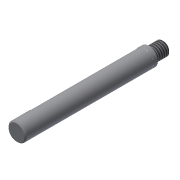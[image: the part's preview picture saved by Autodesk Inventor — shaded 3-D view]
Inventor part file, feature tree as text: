
AUTODESK INVENTOR PART (.ipt)
format: ipt  version: 2015 (Build 190159000, 159)  size: 125,440 bytes
history: native  units: mm
features: extrude x8, sketch x8, chamfer x3, thread x1
ambient origin geometry x8: Origin, YZ Plane, XZ Plane, XY Plane, X Axis, Y Axis, Z Axis, Center Point
bodies: Solid1 (feature_tree)
feature tree (20):
  extrude  "Extrusion1"  Depth=65.0mm TaperAngle=0.0deg
  extrude  "Extrusion2"  Depth=8.5mm TaperAngle=0.0deg
  extrude  "Extrusion3"  Depth=8.5mm TaperAngle=0.0deg
  extrude  "Extrusion4"  Depth=8.5mm TaperAngle=0.0deg
  extrude  "Extrusion5"  Depth=6.0mm
  extrude  "Extrusion6"  Depth=10.0mm TaperAngle=0.0deg
  thread  "Thread1"  [1 undecoded]
  chamfer  "Chamfer1"  Distance=0.5mm Angle=45.0deg
  chamfer  "Chamfer2"  Distance=4.0mm
  extrude  "Extrusion7"  Depth=4.0mm TaperAngle=0.0deg
  extrude  "Extrusion8"  Depth=4.0mm TaperAngle=45.0deg
  chamfer  "Chamfer3"  [1 undecoded]
  sketch  "Sketch1"  dims[d1=6.0mm d2=65.0mm d3=0.0mm]
  sketch  "Sketch2"  dims[d5=8.5mm d6=0.0mm d7=8.5mm d8=0.0mm]
  sketch  "Sketch3"  dims[d9=8.0mm d10=8.5mm d11=0.0mm]
  sketch  "Sketch4"  dims[d12=8.0mm d13=8.5mm d14=0.0mm]
  sketch  "Sketch5"  dims[d15=6.0mm d16=8.0mm]
  sketch  "Sketch6"  dims[d17=6.0mm d18=0.0mm d19=10.0mm d20=0.0mm d21=0.5mm d22=2.0mm d23=45.0deg d24=0.5mm d25=2.0mm d26=45.0deg]
  sketch  "Sketch7"  dims[d27=8.0mm d28=4.0mm d29=0.0mm]
  sketch  "Sketch8"  dims[d30=8.0mm d31=4.0mm d32=0.0mm d33=0.5mm d34=2.0mm d35=45.0deg]
note: 2 required parameter values undecoded (feature->parameter linkage not recoverable at this tier; creation-order binding heuristic only, values carry confidence <= 0.55)
